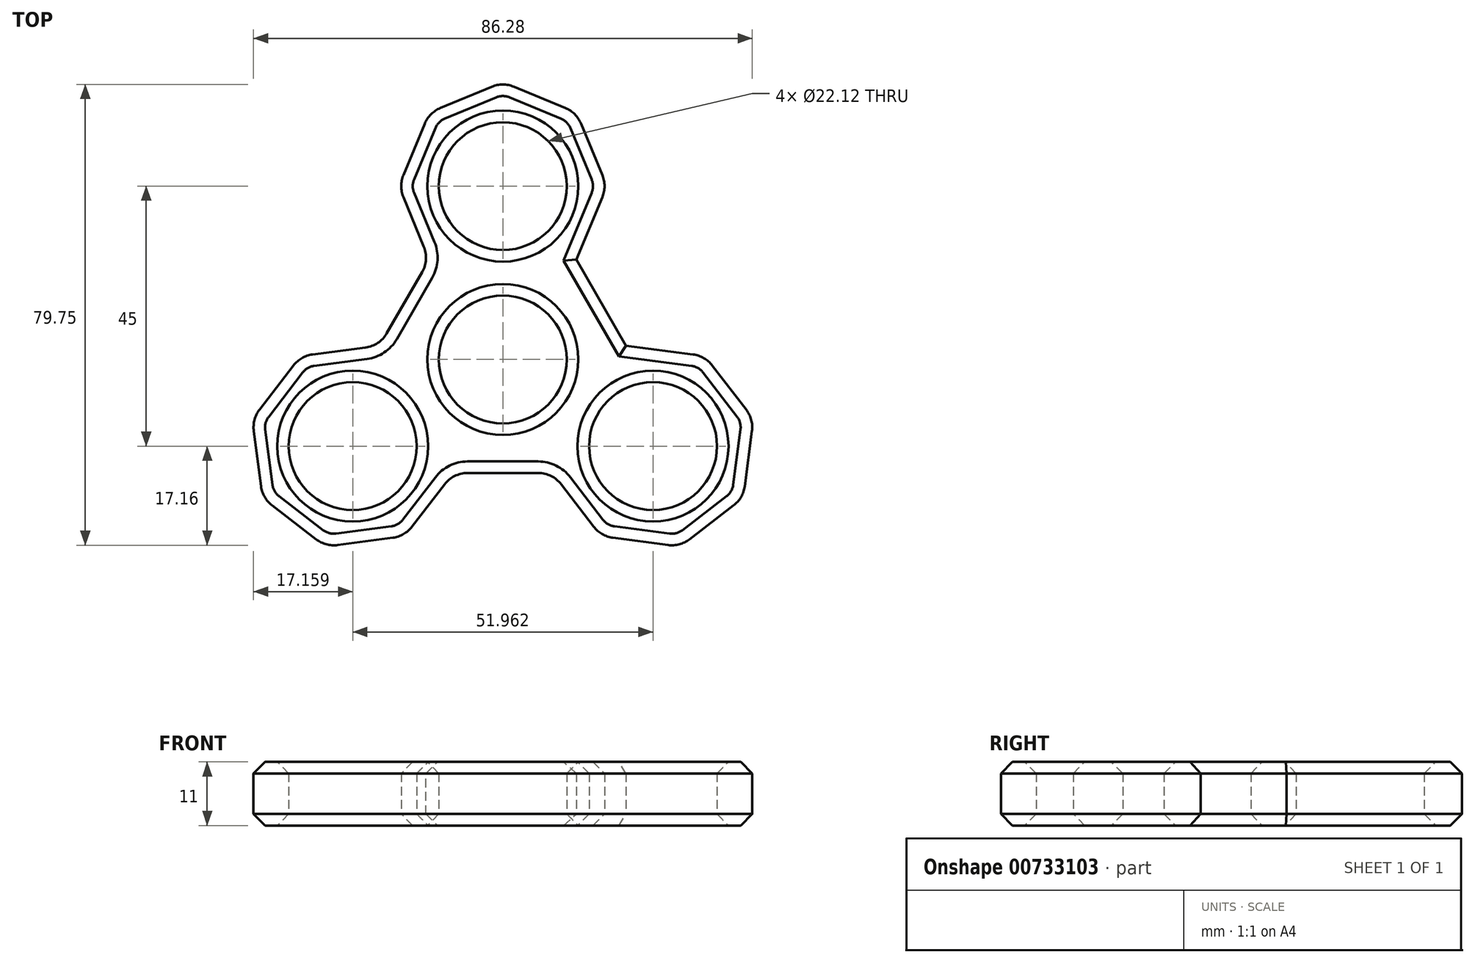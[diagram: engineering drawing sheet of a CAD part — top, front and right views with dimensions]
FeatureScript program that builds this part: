
annotation { "Feature Type Name" : "Feature", "Feature Type Description" : "" }
export const myFeature = defineFeature(function(context is Context, id is Id, definition is map)
    precondition{}
    {
        {
            var Q0;
            Q0=qCreatedBy(makeId("Top.planeOp"),FACE);
            var sketch = newSketch(context, id + "F0", { "sketchPlane" : qUnion([Q0])});
            skCircle(sketch, "E0", {"center": v(0, 0) * mm, "radius": 11.06 * mm});
            skCircle(sketch, "E1", {"center": v(0, 30) * mm, "radius": 11.06 * mm});
            skCircle(sketch, "E2", {"center": v(-25.98, -15) * mm, "radius": 11.06 * mm});
            skCircle(sketch, "E3", {"center": v(25.98, -15) * mm, "radius": 11.06 * mm});
            skLineSegment(sketch, "E4", {"start": v(-25.98, -15) * mm, "end": v(0, 30) * mm, "construction": true});
            skLineSegment(sketch, "E5", {"start": v(25.98, -15) * mm, "end": v(0, 30) * mm, "construction": true});
            skLineSegment(sketch, "E6", {"start": v(25.98, -15) * mm, "end": v(-25.98, -15) * mm, "construction": true});
            skLineSegment(sketch, "E7", {"start": v(25.98, -15) * mm, "end": v(0, 0) * mm, "construction": true});
            skLineSegment(sketch, "E8", {"start": v(0, 0) * mm, "end": v(0, 30) * mm, "construction": true});
            skLineSegment(sketch, "E9", {"start": v(0, 0) * mm, "end": v(-25.98, -15) * mm, "construction": true});
            skLineSegment(sketch, "E10", {"start": v(0, 48) * mm, "end": v(-12.73, 42.73) * mm});
            skLineSegment(sketch, "E11", {"start": v(-12.73, 42.73) * mm, "end": v(-18, 30) * mm});
            skLineSegment(sketch, "E12", {"start": v(-18, 30) * mm, "end": v(-12.73, 17.27) * mm});
            skLineSegment(sketch, "E13", {"start": v(0, 48) * mm, "end": v(12.73, 42.73) * mm});
            skLineSegment(sketch, "E14", {"start": v(12.73, 42.73) * mm, "end": v(18, 30) * mm});
            skLineSegment(sketch, "E15", {"start": v(43.37, -10.34) * mm, "end": v(41.57, -24) * mm});
            skLineSegment(sketch, "E16", {"start": v(41.57, -24) * mm, "end": v(30.64, -32.39) * mm});
            skLineSegment(sketch, "E17", {"start": v(30.64, -32.39) * mm, "end": v(16.98, -30.59) * mm});
            skLineSegment(sketch, "E18", {"start": v(43.37, -10.34) * mm, "end": v(34.98, 0.59) * mm});
            skLineSegment(sketch, "E19", {"start": v(34.98, 0.59) * mm, "end": v(21.32, 2.39) * mm});
            skLineSegment(sketch, "E20", {"start": v(21.32, 2.39) * mm, "end": v(21.32, 2.39) * mm});
            skLineSegment(sketch, "E21", {"start": v(-16.98, -30.59) * mm, "end": v(-30.64, -32.39) * mm});
            skLineSegment(sketch, "E22", {"start": v(-30.64, -32.39) * mm, "end": v(-41.57, -24) * mm});
            skLineSegment(sketch, "E23", {"start": v(-41.57, -24) * mm, "end": v(-43.37, -10.34) * mm});
            skLineSegment(sketch, "E24", {"start": v(-43.37, -10.34) * mm, "end": v(-34.98, 0.59) * mm});
            skLineSegment(sketch, "E25", {"start": v(-34.98, 0.59) * mm, "end": v(-21.32, 2.39) * mm});
            skLineSegment(sketch, "E26", {"start": v(-16.98, -30.59) * mm, "end": v(-8.6, -19.66) * mm});
            skLineSegment(sketch, "E27", {"start": v(16.98, -30.59) * mm, "end": v(8.6, -19.66) * mm});
            skLineSegment(sketch, "E28", {"start": v(-21.32, 2.39) * mm, "end": v(-21.32, 2.39) * mm});
            skLineSegment(sketch, "E29", {"start": v(-8.6, -19.66) * mm, "end": v(8.6, -19.66) * mm});
            skLineSegment(sketch, "E30", {"start": v(18, 30) * mm, "end": v(12.73, 17.27) * mm});
            skLineSegment(sketch, "E31", {"start": v(-12.73, 17.27) * mm, "end": v(-21.32, 2.39) * mm});
            skLineSegment(sketch, "E32", {"start": v(12.73, 17.27) * mm, "end": v(21.32, 2.39) * mm});
            skSolve(sketch);
        }
        {
            var Q0;
            Q0=makeQuery(id+"F0.imprint","IMPRINT",FACE,{"disambiguationData":[TD([[makeQuery(id+"F0.imprint","IMPRINT",EDGE,{"derivedFrom":sQuery(id+"F0.wireOp",EDGE,"E0")}),-1.0]])]});
            extrude(context, id + "F1", {"entities" : qUnion([Q0]), "depth" : 11 * mm, "offsetDistance" : 25 * mm});
        }
        {
            var Q0;
            Q0=makeQuery(id+"F1.opExtrude","SWEPT_EDGE",EDGE,{"disambiguationData":[OSD([sQuery(id+"F0.wireOp",EDGE,"E21"),sQuery(id+"F0.wireOp",EDGE,"E26")])]});
            var Q1;
            Q1=makeQuery(id+"F1.opExtrude","SWEPT_EDGE",EDGE,{"disambiguationData":[OSD([sQuery(id+"F0.wireOp",EDGE,"E21"),sQuery(id+"F0.wireOp",EDGE,"E22")])]});
            var Q2;
            Q2=makeQuery(id+"F1.opExtrude","SWEPT_EDGE",EDGE,{"disambiguationData":[OSD([sQuery(id+"F0.wireOp",EDGE,"E22"),sQuery(id+"F0.wireOp",EDGE,"E23")])]});
            var Q3;
            Q3=makeQuery(id+"F1.opExtrude","SWEPT_EDGE",EDGE,{"disambiguationData":[OSD([sQuery(id+"F0.wireOp",EDGE,"E23"),sQuery(id+"F0.wireOp",EDGE,"E24")])]});
            var Q4;
            Q4=makeQuery(id+"F1.opExtrude","SWEPT_EDGE",EDGE,{"disambiguationData":[OSD([sQuery(id+"F0.wireOp",EDGE,"E24"),sQuery(id+"F0.wireOp",EDGE,"E25")])]});
            var Q5;
            Q5=makeQuery(id+"F1.opExtrude","SWEPT_EDGE",EDGE,{"disambiguationData":[OSD([sQuery(id+"F0.wireOp",EDGE,"E25"),sQuery(id+"F0.wireOp",EDGE,"E28")])]});
            var Q6;
            Q6=makeQuery(id+"F1.opExtrude","SWEPT_EDGE",EDGE,{"disambiguationData":[OSD([sQuery(id+"F0.wireOp",EDGE,"X1Dm3El9-V9QO-N8iI-BB3N-mR4uVBnDAZ1v"),sQuery(id+"F0.wireOp",EDGE,"5tvw3ls0-Of4v-Iv5s-fL3y-tnYmlt4RSaZl")])]});
            var Q7;
            Q7=makeQuery(id+"F1.opExtrude","SWEPT_EDGE",EDGE,{"disambiguationData":[OSD([sQuery(id+"F0.wireOp",EDGE,"E12"),sQuery(id+"F0.wireOp",EDGE,"X1Dm3El9-V9QO-N8iI-BB3N-mR4uVBnDAZ1v")])]});
            var Q8;
            Q8=makeQuery(id+"F1.opExtrude","SWEPT_EDGE",EDGE,{"disambiguationData":[OSD([sQuery(id+"F0.wireOp",EDGE,"E11"),sQuery(id+"F0.wireOp",EDGE,"E12")])]});
            var Q9;
            Q9=makeQuery(id+"F1.opExtrude","SWEPT_EDGE",EDGE,{"disambiguationData":[OSD([sQuery(id+"F0.wireOp",EDGE,"E10"),sQuery(id+"F0.wireOp",EDGE,"E11")])]});
            var Q10;
            Q10=makeQuery(id+"F1.opExtrude","SWEPT_EDGE",EDGE,{"disambiguationData":[OSD([sQuery(id+"F0.wireOp",EDGE,"E10"),sQuery(id+"F0.wireOp",EDGE,"E13")])]});
            var Q11;
            Q11=makeQuery(id+"F1.opExtrude","SWEPT_EDGE",EDGE,{"disambiguationData":[OSD([sQuery(id+"F0.wireOp",EDGE,"E13"),sQuery(id+"F0.wireOp",EDGE,"E14")])]});
            var Q12;
            Q12=makeQuery(id+"F1.opExtrude","SWEPT_EDGE",EDGE,{"disambiguationData":[OSD([sQuery(id+"F0.wireOp",EDGE,"E14"),sQuery(id+"F0.wireOp",EDGE,"tPVarr2a-Sr6X-7oyk-yExZ-pOANCCAjyXez")])]});
            var Q13;
            Q13=makeQuery(id+"F1.opExtrude","SWEPT_EDGE",EDGE,{"disambiguationData":[OSD([sQuery(id+"F0.wireOp",EDGE,"tPVarr2a-Sr6X-7oyk-yExZ-pOANCCAjyXez"),sQuery(id+"F0.wireOp",EDGE,"3JMY6Zoi-zZR4-UiA4-HWqB-pHZLD7yoYNFk")])]});
            var Q14;
            Q14=makeQuery(id+"F1.opExtrude","SWEPT_EDGE",EDGE,{"disambiguationData":[OSD([sQuery(id+"F0.wireOp",EDGE,"E20"),sQuery(id+"F0.wireOp",EDGE,"3JMY6Zoi-zZR4-UiA4-HWqB-pHZLD7yoYNFk")])]});
            var Q15;
            Q15=makeQuery(id+"F1.opExtrude","SWEPT_EDGE",EDGE,{"disambiguationData":[OSD([sQuery(id+"F0.wireOp",EDGE,"E18"),sQuery(id+"F0.wireOp",EDGE,"E19")])]});
            var Q16;
            Q16=makeQuery(id+"F1.opExtrude","SWEPT_EDGE",EDGE,{"disambiguationData":[OSD([sQuery(id+"F0.wireOp",EDGE,"E15"),sQuery(id+"F0.wireOp",EDGE,"E18")])]});
            var Q17;
            Q17=makeQuery(id+"F1.opExtrude","SWEPT_EDGE",EDGE,{"disambiguationData":[OSD([sQuery(id+"F0.wireOp",EDGE,"E15"),sQuery(id+"F0.wireOp",EDGE,"E16")])]});
            var Q18;
            Q18=makeQuery(id+"F1.opExtrude","SWEPT_EDGE",EDGE,{"disambiguationData":[OSD([sQuery(id+"F0.wireOp",EDGE,"E16"),sQuery(id+"F0.wireOp",EDGE,"E17")])]});
            var Q19;
            Q19=makeQuery(id+"F1.opExtrude","SWEPT_EDGE",EDGE,{"disambiguationData":[OSD([sQuery(id+"F0.wireOp",EDGE,"E17"),sQuery(id+"F0.wireOp",EDGE,"E27")])]});
            var Q20;
            Q20=makeQuery(id+"F1.opExtrude","SWEPT_EDGE",EDGE,{"disambiguationData":[OSD([sQuery(id+"F0.wireOp",EDGE,"E27"),sQuery(id+"F0.wireOp",EDGE,"E29")])]});
            var Q21;
            Q21=makeQuery(id+"F1.opExtrude","SWEPT_EDGE",EDGE,{"disambiguationData":[OSD([sQuery(id+"F0.wireOp",EDGE,"E26"),sQuery(id+"F0.wireOp",EDGE,"E29")])]});
            fillet(context, id + "F2", {"entities" : qUnion([Q0, Q1, Q2, Q3, Q4, Q5, Q6, Q7, Q8, Q9, Q10, Q11, Q12, Q13, Q14, Q15, Q16, Q17, Q18, Q19, Q20, Q21]), "radius" : 5 * mm, "tangentPropagation" : true, "allowEdgeOverflow" : false});
        }
        {
            var Q0;
            Q0=makeQuery(id+"F1.opExtrude","CAP_FACE",FACE,{"disambiguationData":[OSD([sQuery(id+"F0.wireOp",EDGE,"E0"),sQuery(id+"F0.wireOp",EDGE,"E1"),sQuery(id+"F0.wireOp",EDGE,"E2"),sQuery(id+"F0.wireOp",EDGE,"E3"),sQuery(id+"F0.wireOp",EDGE,"E10"),sQuery(id+"F0.wireOp",EDGE,"E11"),sQuery(id+"F0.wireOp",EDGE,"E12"),sQuery(id+"F0.wireOp",EDGE,"X1Dm3El9-V9QO-N8iI-BB3N-mR4uVBnDAZ1v"),sQuery(id+"F0.wireOp",EDGE,"E13"),sQuery(id+"F0.wireOp",EDGE,"E14"),sQuery(id+"F0.wireOp",EDGE,"tPVarr2a-Sr6X-7oyk-yExZ-pOANCCAjyXez"),sQuery(id+"F0.wireOp",EDGE,"E15"),sQuery(id+"F0.wireOp",EDGE,"E16"),sQuery(id+"F0.wireOp",EDGE,"E17"),sQuery(id+"F0.wireOp",EDGE,"E18"),sQuery(id+"F0.wireOp",EDGE,"E19"),sQuery(id+"F0.wireOp",EDGE,"E20"),sQuery(id+"F0.wireOp",EDGE,"E21"),sQuery(id+"F0.wireOp",EDGE,"E22"),sQuery(id+"F0.wireOp",EDGE,"E23"),sQuery(id+"F0.wireOp",EDGE,"E24"),sQuery(id+"F0.wireOp",EDGE,"E25"),sQuery(id+"F0.wireOp",EDGE,"E26"),sQuery(id+"F0.wireOp",EDGE,"E27"),sQuery(id+"F0.wireOp",EDGE,"E28"),sQuery(id+"F0.wireOp",EDGE,"E29"),sQuery(id+"F0.wireOp",EDGE,"3JMY6Zoi-zZR4-UiA4-HWqB-pHZLD7yoYNFk"),sQuery(id+"F0.wireOp",EDGE,"5tvw3ls0-Of4v-Iv5s-fL3y-tnYmlt4RSaZl")])],"isStart":false});
            chamfer(context, id + "F3", {"entities" : qUnion([Q0]), "width" : 2 * mm, "tangentPropagation" : true});
        }
        {
            var Q0;
            Q0=makeQuery(id+"F1.opExtrude","CAP_FACE",FACE,{"disambiguationData":[OSD([sQuery(id+"F0.wireOp",EDGE,"E0"),sQuery(id+"F0.wireOp",EDGE,"E1"),sQuery(id+"F0.wireOp",EDGE,"E2"),sQuery(id+"F0.wireOp",EDGE,"E3"),sQuery(id+"F0.wireOp",EDGE,"E10"),sQuery(id+"F0.wireOp",EDGE,"E11"),sQuery(id+"F0.wireOp",EDGE,"E12"),sQuery(id+"F0.wireOp",EDGE,"X1Dm3El9-V9QO-N8iI-BB3N-mR4uVBnDAZ1v"),sQuery(id+"F0.wireOp",EDGE,"E13"),sQuery(id+"F0.wireOp",EDGE,"E14"),sQuery(id+"F0.wireOp",EDGE,"tPVarr2a-Sr6X-7oyk-yExZ-pOANCCAjyXez"),sQuery(id+"F0.wireOp",EDGE,"E15"),sQuery(id+"F0.wireOp",EDGE,"E16"),sQuery(id+"F0.wireOp",EDGE,"E17"),sQuery(id+"F0.wireOp",EDGE,"E18"),sQuery(id+"F0.wireOp",EDGE,"E19"),sQuery(id+"F0.wireOp",EDGE,"E20"),sQuery(id+"F0.wireOp",EDGE,"E21"),sQuery(id+"F0.wireOp",EDGE,"E22"),sQuery(id+"F0.wireOp",EDGE,"E23"),sQuery(id+"F0.wireOp",EDGE,"E24"),sQuery(id+"F0.wireOp",EDGE,"E25"),sQuery(id+"F0.wireOp",EDGE,"E26"),sQuery(id+"F0.wireOp",EDGE,"E27"),sQuery(id+"F0.wireOp",EDGE,"E28"),sQuery(id+"F0.wireOp",EDGE,"E29"),sQuery(id+"F0.wireOp",EDGE,"3JMY6Zoi-zZR4-UiA4-HWqB-pHZLD7yoYNFk"),sQuery(id+"F0.wireOp",EDGE,"5tvw3ls0-Of4v-Iv5s-fL3y-tnYmlt4RSaZl")])],"isStart":true});
            chamfer(context, id + "F4", {"entities" : qUnion([Q0]), "width" : 2 * mm, "tangentPropagation" : true});
        }
    });
